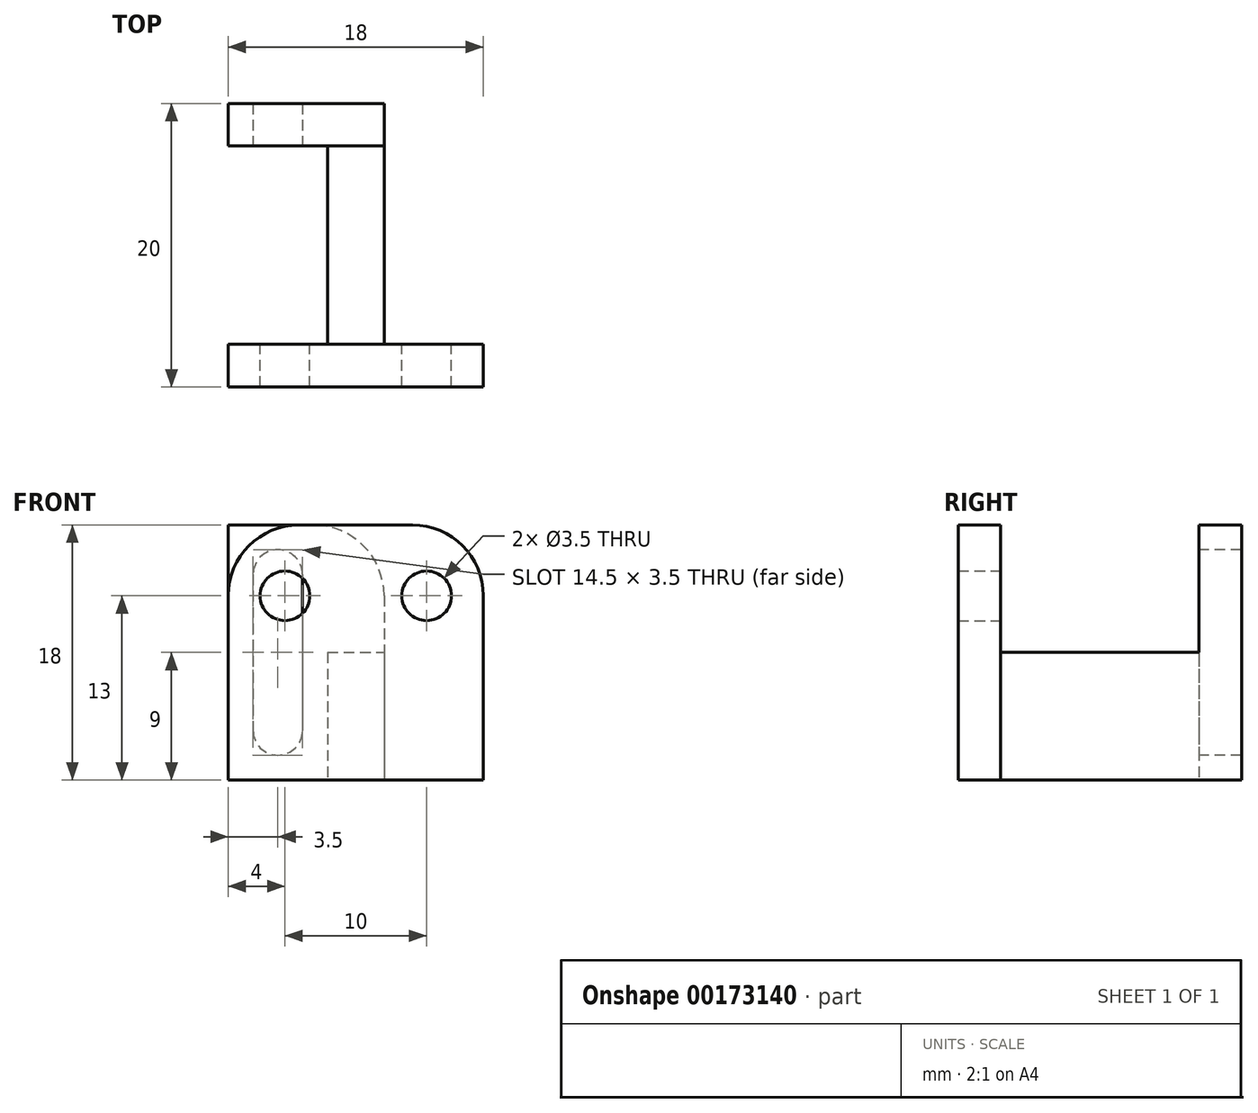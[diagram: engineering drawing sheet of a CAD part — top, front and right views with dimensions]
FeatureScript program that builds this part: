
annotation { "Feature Type Name" : "Feature", "Feature Type Description" : "" }
export const myFeature = defineFeature(function(context is Context, id is Id, definition is map)
    precondition{}
    {
        {
            var Q0;
            Q0=qCreatedBy(makeId("Front.planeOp"),FACE);
            var sketch = newSketch(context, id + "F0", { "sketchPlane" : qUnion([Q0])});
            skLineSegment(sketch, "E0.top", {"start": v(-9, -9) * mm, "end": v(9, -9) * mm});
            skLineSegment(sketch, "E0.left", {"start": v(-9, 9) * mm, "end": v(-9, -9) * mm});
            skLineSegment(sketch, "E0.right", {"start": v(9, 9) * mm, "end": v(9, -9) * mm});
            skPoint(sketch, "E1", {"position": v(-5, 13) * mm});
            skPoint(sketch, "E2", {"position": v(0, 9) * mm});
            skPoint(sketch, "E3", {"position": v(9, 0) * mm});
            skLineSegment(sketch, "E4", {"start": v(-5, 13) * mm, "end": v(5, 13) * mm});
            skPoint(sketch, "E5", {"position": v(0, 13) * mm});
            skLineSegment(sketch, "E6", {"start": v(9, 0) * mm, "end": v(-9, 0) * mm});
            skLineSegment(sketch, "E7", {"start": v(-9, 9) * mm, "end": v(-9, 18) * mm});
            skLineSegment(sketch, "E8", {"start": v(-9, 18) * mm, "end": v(9, 18) * mm});
            skLineSegment(sketch, "E9", {"start": v(9, 18) * mm, "end": v(9, 9) * mm});
            skSolve(sketch);
        }
        {
            var Q0;
            {var subQ1=sQuery(id+"F0.wireOp",EDGE,"E6");Q0=makeQuery(id+"F0.imprint","IMPRINT",FACE,{"disambiguationData":[TD([[makeQuery(id+"F0.imprint","IMPRINT",EDGE,{"derivedFrom":subQ1}),-1.0]])]});}
            extrude(context, id + "F1", {"entities" : qUnion([Q0]), "depth" : 3 * mm});
        }
        {
            var Q0;
            Q0=sQuery(id+"F0.wireOp",VERTEX,"E1");
            var Q1;
            Q1=sQuery(id+"F0.wireOp",VERTEX,"E4.end");
            var Q2;
            Q2=makeQuery(id+"F1.opExtrude","SWEPT_BODY",BODY,{"disambiguationData":[OSD([sQuery(id+"F0.wireOp",EDGE,"E0.bottom"),sQuery(id+"F0.wireOp",EDGE,"E0.top"),sQuery(id+"F0.wireOp",EDGE,"E0.left"),sQuery(id+"F0.wireOp",EDGE,"E0.right")])]});
            hole(context, id + "F2", {"style" : HoleStyle.SIMPLE, "endStyle" : HoleEndStyle.THROUGH, "oppositeDirection" : true, "holeDiameter" : 3.5 * mm, "startFromSketch" : true, "locations" : qUnion([Q0, Q1]), "scope" : qUnion([Q2]), "isTappedThrough" : true});
        }
        {
            var Q0;
            {var subQ1=sQuery(id+"F0.wireOp",EDGE,"E6");Q0=makeQuery(id+"F0.imprint","IMPRINT",FACE,{"disambiguationData":[TD([[makeQuery(id+"F0.imprint","IMPRINT",EDGE,{"derivedFrom":subQ1}),-1.0]])]});}
            var sketch = newSketch(context, id + "F3", { "sketchPlane" : qUnion([Q0])});
            skLineSegment(sketch, "E10.0", {"start": v(-9, 9) * mm, "end": v(9, 9) * mm, "construction": true});
            skLineSegment(sketch, "E11.bottom", {"start": v(-2, 9) * mm, "end": v(2, 9) * mm});
            skLineSegment(sketch, "E11.top", {"start": v(-2, 0) * mm, "end": v(2, 0) * mm});
            skLineSegment(sketch, "E11.left", {"start": v(-2, 9) * mm, "end": v(-2, 0) * mm});
            skLineSegment(sketch, "E11.right", {"start": v(2, 9) * mm, "end": v(2, 0) * mm});
            skPoint(sketch, "E12", {"position": v(0, 0) * mm});
            skSolve(sketch);
        }
        {
            var Q0;
            Q0=makeQuery(id+"F3.imprint","IMPRINT",FACE,{"disambiguationData":[TD([[makeQuery(id+"F3.imprint","IMPRINT",EDGE,{"derivedFrom":sQuery(id+"F3.wireOp",EDGE,"E11.bottom")}),-1.0]])]});
            extrude(context, id + "F4", {"entities" : qUnion([Q0]), "operationType" : NewBodyOperationType.ADD, "oppositeDirection" : true, "depth" : 14 * mm});
        }
        {
            var Q0;
            Q0=makeQuery(id+"F4.opExtrude","CAP_FACE",FACE,{"disambiguationData":[OSD([sQuery(id+"F3.wireOp",EDGE,"E11.bottom"),sQuery(id+"F3.wireOp",EDGE,"E11.top"),sQuery(id+"F3.wireOp",EDGE,"E11.left"),sQuery(id+"F3.wireOp",EDGE,"E11.right")])],"isStart":false});
            var sketch = newSketch(context, id + "F5", { "sketchPlane" : qUnion([Q0])});
            skLineSegment(sketch, "E13.0", {"start": v(2, 9) * mm, "end": v(-2, 9) * mm, "construction": true});
            skLineSegment(sketch, "E14.bottom", {"start": v(9, 18) * mm, "end": v(-2, 18) * mm});
            skLineSegment(sketch, "E14.top", {"start": v(9, 0) * mm, "end": v(-2, 0) * mm});
            skLineSegment(sketch, "E14.left", {"start": v(9, 18) * mm, "end": v(9, 0) * mm});
            skLineSegment(sketch, "E14.right", {"start": v(-2, 18) * mm, "end": v(-2, 0) * mm});
            skLineSegment(sketch, "E15.bottom", {"start": v(5.5, 16.25) * mm, "end": v(5.5, 16.25) * mm});
            skLineSegment(sketch, "E15.top", {"start": v(5.5, 1.75) * mm, "end": v(5.5, 1.75) * mm});
            skLineSegment(sketch, "E15.left", {"start": v(7.25, 14.5) * mm, "end": v(7.25, 3.5) * mm});
            skLineSegment(sketch, "E15.right", {"start": v(3.75, 14.5) * mm, "end": v(3.75, 3.5) * mm});
            skLineSegment(sketch, "E16", {"start": v(2, 9) * mm, "end": v(9, 9) * mm, "construction": true});
            skPoint(sketch, "E17", {"position": v(5.5, 16.25) * mm});
            skPoint(sketch, "E18", {"position": v(5.5, 9) * mm});
            skPoint(sketch, "E19", {"position": v(9, 9) * mm});
            skPoint(sketch, "E19.positionSnap0", {"position": v(7.25, 9) * mm});
            skPoint(sketch, "E20.visualSharp", {"position": v(7.25, 16.25) * mm});
            skArc(sketch, "E20.filletArc", {"start": v(7.25, 14.5) * mm, "mid": v(6.74, 15.74) * mm, "end": v(5.5, 16.25) * mm});
            skPoint(sketch, "E21.visualSharp", {"position": v(3.75, 16.25) * mm});
            skArc(sketch, "E21.filletArc", {"start": v(5.5, 16.25) * mm, "mid": v(4.26, 15.74) * mm, "end": v(3.75, 14.5) * mm});
            skPoint(sketch, "E22.visualSharp", {"position": v(3.75, 1.75) * mm});
            skArc(sketch, "E22.filletArc", {"start": v(3.75, 3.5) * mm, "mid": v(4.26, 2.26) * mm, "end": v(5.5, 1.75) * mm});
            skPoint(sketch, "E23.visualSharp", {"position": v(7.25, 1.75) * mm});
            skArc(sketch, "E23.filletArc", {"start": v(5.5, 1.75) * mm, "mid": v(6.74, 2.26) * mm, "end": v(7.25, 3.5) * mm});
            skSolve(sketch);
        }
        {
            var Q0;
            {var subQ0=sQuery(id+"F5.wireOp",EDGE,"E14.bottom");Q0=makeQuery(id+"F5.imprint","IMPRINT",FACE,{"disambiguationData":[TD([[makeQuery(id+"F5.imprint","IMPRINT",EDGE,{"derivedFrom":subQ0}),1.0]])]});}
            var Q1;
            {var subQ4=makeQuery(id+"F4.opExtrude","CAP_EDGE",EDGE,{"disambiguationData":[OSD([sQuery(id+"F3.wireOp",EDGE,"E11.bottom")])],"isStart":false});Q1=makeQuery(id+"F5.imprint","IMPRINT",FACE,{"disambiguationData":[TD([[makeQuery(id+"F5.imprint","IMPRINT",EDGE,{"derivedFrom":subQ4}),1.0]])]});}
            extrude(context, id + "F6", {"entities" : qUnion([Q0, Q1]), "operationType" : NewBodyOperationType.ADD, "depth" : 3 * mm});
        }
        {
            var Q0;
            Q0=makeQuery(id+"F1.opExtrude","SWEPT_EDGE",EDGE,{"disambiguationData":[OSD([sQuery(id+"F0.wireOp",EDGE,"E8"),sQuery(id+"F0.wireOp",EDGE,"E9")])]});
            var Q1;
            Q1=makeQuery(id+"F1.opExtrude","SWEPT_EDGE",EDGE,{"disambiguationData":[OSD([sQuery(id+"F0.wireOp",EDGE,"E7"),sQuery(id+"F0.wireOp",EDGE,"E8")])]});
            var Q2;
            Q2=makeQuery(id+"F6.opExtrude","SWEPT_EDGE",EDGE,{"disambiguationData":[OSD([sQuery(id+"F5.wireOp",EDGE,"E14.bottom"),sQuery(id+"F5.wireOp",EDGE,"E14.right")])]});
            fillet(context, id + "F7", {"entities" : qUnion([Q0, Q1, Q2]), "radius" : 5 * mm, "tangentPropagation" : true, "allowEdgeOverflow" : false});
        }
    });
